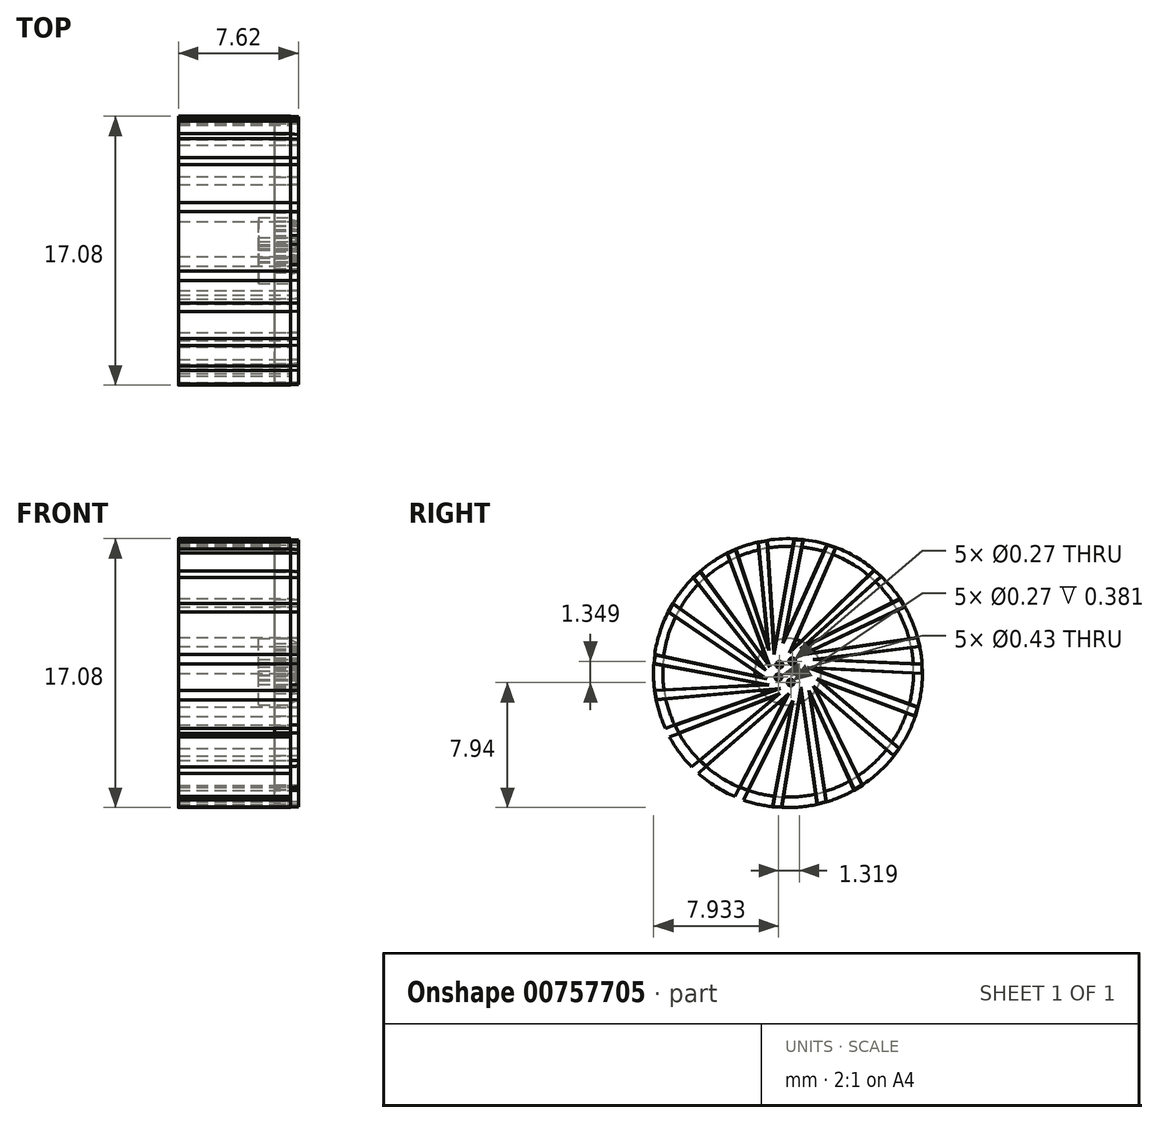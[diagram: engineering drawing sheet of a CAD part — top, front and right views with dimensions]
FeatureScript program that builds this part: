
annotation { "Feature Type Name" : "Feature", "Feature Type Description" : "" }
export const myFeature = defineFeature(function(context is Context, id is Id, definition is map)
    precondition{}
    {
        {
            var Q0;
            Q0=qCreatedBy(makeId("Right.planeOp"),FACE);
            var sketch = newSketch(context, id + "F0", { "sketchPlane" : qUnion([Q0])});
            skCircle(sketch, "E0", {"center": v(-0.01, -0.1) * mm, "radius": 8.54 * mm});
            skCircle(sketch, "E1", {"center": v(0, 0) * mm, "radius": 2.1 * mm});
            skCircle(sketch, "E2", {"center": v(0, 0) * mm, "radius": 7.96 * mm});
            skLineSegment(sketch, "E3", {"start": v(-0.39, -8.62) * mm, "end": v(0.81, -1.16) * mm});
            skLineSegment(sketch, "E4", {"start": v(0.81, -1.16) * mm, "end": v(1.84, -8.43) * mm});
            skLineSegment(sketch, "E5", {"start": v(2.43, -8.27) * mm, "end": v(1.38, -1.38) * mm});
            skLineSegment(sketch, "E6", {"start": v(1.38, -1.38) * mm, "end": v(4.19, -7.53) * mm});
            skLineSegment(sketch, "E7", {"start": v(-1, -8.58) * mm, "end": v(0.24, -2) * mm});
            skLineSegment(sketch, "E8", {"start": v(0.24, -2) * mm, "end": v(-2.83, -8.16) * mm});
            skLineSegment(sketch, "E9", {"start": v(-2.83, -8.16) * mm, "end": v(-3.4, -7.93) * mm});
            skLineSegment(sketch, "E10", {"start": v(-3.4, -7.93) * mm, "end": v(-0.05, -1.48) * mm});
            skLineSegment(sketch, "E11", {"start": v(-0.05, -1.48) * mm, "end": v(-5.7, -6.46) * mm});
            skLineSegment(sketch, "E12", {"start": v(-5.7, -6.46) * mm, "end": v(-6.14, -6.04) * mm});
            skLineSegment(sketch, "E13", {"start": v(-6.14, -6.04) * mm, "end": v(-0.66, -1.47) * mm});
            skLineSegment(sketch, "E14", {"start": v(-0.66, -1.47) * mm, "end": v(-7.53, -4.14) * mm});
            skLineSegment(sketch, "E15", {"start": v(-7.53, -4.14) * mm, "end": v(-7.8, -3.6) * mm});
            skLineSegment(sketch, "E16", {"start": v(-7.8, -3.6) * mm, "end": v(-0.7, -1.1) * mm});
            skLineSegment(sketch, "E17", {"start": v(-0.7, -1.1) * mm, "end": v(-8.39, -1.78) * mm});
            skLineSegment(sketch, "E18", {"start": v(-8.48, -1.18) * mm, "end": v(-1.45, -0.82) * mm});
            skLineSegment(sketch, "E19", {"start": v(-1.45, -0.82) * mm, "end": v(-8.53, 0.5) * mm});
            skLineSegment(sketch, "E20", {"start": v(-8.47, 1.1) * mm, "end": v(-1.46, -0.4) * mm});
            skLineSegment(sketch, "E21", {"start": v(-1.46, -0.4) * mm, "end": v(-7.62, 3.8) * mm});
            skLineSegment(sketch, "E22", {"start": v(-7.32, 4.33) * mm, "end": v(-1.54, 0.2) * mm});
            skLineSegment(sketch, "E23", {"start": v(-1.54, 0.2) * mm, "end": v(-6.03, 5.97) * mm});
            skLineSegment(sketch, "E24", {"start": v(-5.58, 6.38) * mm, "end": v(-1.25, 0.47) * mm});
            skLineSegment(sketch, "E25", {"start": v(4.7, -7.2) * mm, "end": v(1.68, -1) * mm});
            skLineSegment(sketch, "E26", {"start": v(1.68, -1) * mm, "end": v(6.7, -5.36) * mm});
            skLineSegment(sketch, "E27", {"start": v(7.06, -4.87) * mm, "end": v(1.98, -0.54) * mm});
            skLineSegment(sketch, "E28", {"start": v(1.98, -0.54) * mm, "end": v(8.07, -2.83) * mm});
            skLineSegment(sketch, "E29", {"start": v(8.5, 0.48) * mm, "end": v(1.87, 0.78) * mm});
            skLineSegment(sketch, "E30", {"start": v(1.87, 0.78) * mm, "end": v(8.36, 1.6) * mm});
            skLineSegment(sketch, "E31", {"start": v(8.22, 2.19) * mm, "end": v(1.05, 1.12) * mm});
            skLineSegment(sketch, "E32", {"start": v(1.05, 1.12) * mm, "end": v(7.42, 4.12) * mm});
            skLineSegment(sketch, "E33", {"start": v(7.1, 4.64) * mm, "end": v(0.95, 1.57) * mm});
            skLineSegment(sketch, "E34", {"start": v(0.95, 1.57) * mm, "end": v(5.92, 6.05) * mm});
            skLineSegment(sketch, "E35", {"start": v(5.46, 6.46) * mm, "end": v(0.17, 1.3) * mm});
            skLineSegment(sketch, "E36", {"start": v(0.17, 1.3) * mm, "end": v(3.04, 7.88) * mm});
            skLineSegment(sketch, "E37", {"start": v(2.47, 8.08) * mm, "end": v(-0.26, 2.01) * mm});
            skLineSegment(sketch, "E38", {"start": v(-0.26, 2.01) * mm, "end": v(0.99, 8.39) * mm});
            skLineSegment(sketch, "E39", {"start": v(0.38, 8.39) * mm, "end": v(-0.88, 1.31) * mm});
            skLineSegment(sketch, "E40", {"start": v(-0.88, 1.31) * mm, "end": v(-1.3, 8.35) * mm});
            skLineSegment(sketch, "E41", {"start": v(-1.9, 8.24) * mm, "end": v(-1.28, 1.57) * mm});
            skLineSegment(sketch, "E42", {"start": v(-1.28, 1.57) * mm, "end": v(-3.32, 7.78) * mm});
            skLineSegment(sketch, "E43", {"start": v(-3.87, 7.53) * mm, "end": v(-1.25, 0.47) * mm});
            skLineSegment(sketch, "E44", {"start": v(-1.9, 8.24) * mm, "end": v(-1.3, 8.35) * mm});
            skLineSegment(sketch, "E45", {"start": v(0.38, 8.39) * mm, "end": v(0.99, 8.39) * mm});
            skLineSegment(sketch, "E46", {"start": v(2.47, 8.08) * mm, "end": v(3.04, 7.88) * mm});
            skLineSegment(sketch, "E47", {"start": v(-3.32, 7.78) * mm, "end": v(-3.87, 7.53) * mm});
            skLineSegment(sketch, "E48", {"start": v(-5.58, 6.38) * mm, "end": v(-6.03, 5.97) * mm});
            skLineSegment(sketch, "E49", {"start": v(-7.32, 4.33) * mm, "end": v(-7.62, 3.8) * mm});
            skLineSegment(sketch, "E50", {"start": v(-7.8, -3.6) * mm, "end": v(-7.53, -4.14) * mm});
            skLineSegment(sketch, "E51", {"start": v(-6.14, -6.04) * mm, "end": v(-5.7, -6.46) * mm});
            skLineSegment(sketch, "E52", {"start": v(-3.4, -7.93) * mm, "end": v(-2.83, -8.16) * mm});
            skLineSegment(sketch, "E53", {"start": v(-1, -8.58) * mm, "end": v(-0.39, -8.62) * mm});
            skLineSegment(sketch, "E54", {"start": v(1.84, -8.43) * mm, "end": v(2.43, -8.27) * mm});
            skLineSegment(sketch, "E55", {"start": v(4.19, -7.53) * mm, "end": v(4.7, -7.2) * mm});
            skLineSegment(sketch, "E56", {"start": v(6.7, -5.36) * mm, "end": v(7.06, -4.87) * mm});
            skLineSegment(sketch, "E57", {"start": v(8.53, -0.13) * mm, "end": v(8.5, 0.48) * mm});
            skLineSegment(sketch, "E58", {"start": v(8.36, 1.6) * mm, "end": v(8.22, 2.19) * mm});
            skLineSegment(sketch, "E59", {"start": v(7.1, 4.64) * mm, "end": v(7.42, 4.12) * mm});
            skLineSegment(sketch, "E60", {"start": v(5.46, 6.46) * mm, "end": v(5.92, 6.05) * mm});
            skLineSegment(sketch, "E61", {"start": v(-8.47, 1.1) * mm, "end": v(-8.53, 0.5) * mm});
            skLineSegment(sketch, "E62", {"start": v(-8.39, -1.78) * mm, "end": v(-8.48, -1.18) * mm});
            skLineSegment(sketch, "E63", {"start": v(1.4, 0.23) * mm, "end": v(8.25, -2.25) * mm});
            skLineSegment(sketch, "E64", {"start": v(1.4, 0.23) * mm, "end": v(8.53, -0.13) * mm});
            skLineSegment(sketch, "E65", {"start": v(8.25, -2.25) * mm, "end": v(8.07, -2.83) * mm});
            skCircle(sketch, "E66", {"center": v(0, 0) * mm, "radius": 0.52 * mm});
            skCircle(sketch, "E67", {"center": v(0.26, 0.66) * mm, "radius": 0.19 * mm});
            skCircle(sketch, "E68", {"center": v(-0.55, 0.44) * mm, "radius": 0.19 * mm});
            skCircle(sketch, "E69", {"center": v(0.7, -0.1) * mm, "radius": 0.19 * mm});
            skCircle(sketch, "E70", {"center": v(-0.62, -0.35) * mm, "radius": 0.19 * mm});
            skCircle(sketch, "E71", {"center": v(0.16, -0.69) * mm, "radius": 0.19 * mm});
            skCircle(sketch, "E72", {"center": v(0.26, 0.66) * mm, "radius": 0.13 * mm});
            skCircle(sketch, "E73", {"center": v(-0.55, 0.44) * mm, "radius": 0.13 * mm});
            skCircle(sketch, "E74", {"center": v(-0.62, -0.35) * mm, "radius": 0.13 * mm});
            skCircle(sketch, "E75", {"center": v(0.16, -0.69) * mm, "radius": 0.13 * mm});
            skCircle(sketch, "E76", {"center": v(0.7, -0.1) * mm, "radius": 0.13 * mm});
            skLineSegment(sketch, "E77", {"start": v(-2, -1.56) * mm, "end": v(-1.87, -1.94) * mm});
            skLineSegment(sketch, "E78", {"start": v(-1.64, -2.3) * mm, "end": v(-1.36, -2.64) * mm});
            skLineSegment(sketch, "E79", {"start": v(-0.76, -2.86) * mm, "end": v(-0.3, -3.1) * mm});
            skLineSegment(sketch, "E80", {"start": v(0.04, -3.1) * mm, "end": v(0.49, -3.18) * mm});
            skLineSegment(sketch, "E81", {"start": v(1.1, -3.26) * mm, "end": v(1.66, -3.18) * mm});
            skLineSegment(sketch, "E82", {"start": v(2.12, -2.99) * mm, "end": v(2.55, -2.78) * mm});
            skLineSegment(sketch, "E83", {"start": v(3.07, -2.21) * mm, "end": v(3.44, -1.78) * mm});
            skLineSegment(sketch, "E84", {"start": v(3.64, -1.17) * mm, "end": v(3.74, -0.61) * mm});
            skLineSegment(sketch, "E85", {"start": v(-2.23, -1.23) * mm, "end": v(-2.25, -0.86) * mm});
            skLineSegment(sketch, "E86", {"start": v(-2.49, -0.62) * mm, "end": v(-2.4, -0.2) * mm});
            skLineSegment(sketch, "E87", {"start": v(-2.6, 0.38) * mm, "end": v(-2.33, 0.76) * mm});
            skLineSegment(sketch, "E88", {"start": v(-2.26, 1.12) * mm, "end": v(-1.91, 1.37) * mm});
            skLineSegment(sketch, "E89", {"start": v(-1.76, 1.84) * mm, "end": v(-1.4, 1.96) * mm});
            skSolve(sketch);
        }
        {
            var Q0;
            {var subQ36=sQuery(id+"F0.wireOp",EDGE,"E67");Q0=makeQuery(id+"F0.imprint","IMPRINT",FACE,{"disambiguationData":[TD([[makeQuery(id+"F0.imprint","IMPRINT",EDGE,{"derivedFrom":subQ36}),-1.0]])]});}
            var Q1;
            {var subQ0=sQuery(id+"F0.wireOp",EDGE,"E32");var subQ1=sQuery(id+"F0.wireOp",EDGE,"E1");var subQ2=makeQuery(id+"F0.imprint","INTERSECT",VERTEX,{"derivedFrom":[subQ1,subQ0]});Q1=makeQuery(id+"F0.imprint","IMPRINT",FACE,{"disambiguationData":[TD([[makeQuery(id+"F0.imprint","IMPRINT",EDGE,{"disambiguationData":[TD([[subQ2,-1.0]])],"derivedFrom":subQ1}),-1.0]])]});}
            var Q2;
            {var subQ0=sQuery(id+"F0.wireOp",EDGE,"E34");var subQ1=sQuery(id+"F0.wireOp",EDGE,"E1");var subQ2=makeQuery(id+"F0.imprint","INTERSECT",VERTEX,{"derivedFrom":[subQ1,subQ0]});Q2=makeQuery(id+"F0.imprint","IMPRINT",FACE,{"disambiguationData":[TD([[makeQuery(id+"F0.imprint","IMPRINT",EDGE,{"disambiguationData":[TD([[subQ2,-1.0]])],"derivedFrom":subQ1}),-1.0]])]});}
            var Q3;
            {var subQ0=sQuery(id+"F0.wireOp",EDGE,"E36");var subQ1=sQuery(id+"F0.wireOp",EDGE,"E1");var subQ2=makeQuery(id+"F0.imprint","INTERSECT",VERTEX,{"derivedFrom":[subQ1,subQ0]});Q3=makeQuery(id+"F0.imprint","IMPRINT",FACE,{"disambiguationData":[TD([[makeQuery(id+"F0.imprint","IMPRINT",EDGE,{"disambiguationData":[TD([[subQ2,-1.0]])],"derivedFrom":subQ1}),-1.0]])]});}
            var Q4;
            {var subQ0=sQuery(id+"F0.wireOp",EDGE,"E38");var subQ1=sQuery(id+"F0.wireOp",EDGE,"E1");var subQ2=makeQuery(id+"F0.imprint","INTERSECT",VERTEX,{"derivedFrom":[subQ1,subQ0]});Q4=makeQuery(id+"F0.imprint","IMPRINT",FACE,{"disambiguationData":[TD([[makeQuery(id+"F0.imprint","IMPRINT",EDGE,{"disambiguationData":[TD([[subQ2,-1.0]])],"derivedFrom":subQ1}),-1.0]])]});}
            var Q5;
            {var subQ0=sQuery(id+"F0.wireOp",EDGE,"E30");var subQ1=sQuery(id+"F0.wireOp",EDGE,"E1");var subQ2=makeQuery(id+"F0.imprint","INTERSECT",VERTEX,{"derivedFrom":[subQ1,subQ0]});Q5=makeQuery(id+"F0.imprint","IMPRINT",FACE,{"disambiguationData":[TD([[makeQuery(id+"F0.imprint","IMPRINT",EDGE,{"disambiguationData":[TD([[subQ2,-1.0]])],"derivedFrom":subQ1}),-1.0]])]});}
            var Q6;
            {var subQ0=sQuery(id+"F0.wireOp",EDGE,"E29");var subQ1=sQuery(id+"F0.wireOp",EDGE,"E1");var subQ2=makeQuery(id+"F0.imprint","INTERSECT",VERTEX,{"derivedFrom":[subQ1,subQ0]});Q6=makeQuery(id+"F0.imprint","IMPRINT",FACE,{"disambiguationData":[TD([[makeQuery(id+"F0.imprint","IMPRINT",EDGE,{"disambiguationData":[TD([[subQ2,1.0]])],"derivedFrom":subQ1}),-1.0]])]});}
            var Q7;
            {var subQ0=sQuery(id+"F0.wireOp",EDGE,"E28");var subQ1=sQuery(id+"F0.wireOp",EDGE,"E1");var subQ2=makeQuery(id+"F0.imprint","INTERSECT",VERTEX,{"derivedFrom":[subQ1,subQ0]});Q7=makeQuery(id+"F0.imprint","IMPRINT",FACE,{"disambiguationData":[TD([[makeQuery(id+"F0.imprint","IMPRINT",EDGE,{"disambiguationData":[TD([[subQ2,-1.0]])],"derivedFrom":subQ1}),-1.0]])]});}
            var Q8;
            {var subQ0=sQuery(id+"F0.wireOp",EDGE,"E26");var subQ1=sQuery(id+"F0.wireOp",EDGE,"E1");var subQ2=makeQuery(id+"F0.imprint","INTERSECT",VERTEX,{"derivedFrom":[subQ1,subQ0]});Q8=makeQuery(id+"F0.imprint","IMPRINT",FACE,{"disambiguationData":[TD([[makeQuery(id+"F0.imprint","IMPRINT",EDGE,{"disambiguationData":[TD([[subQ2,-1.0]])],"derivedFrom":subQ1}),-1.0]])]});}
            var Q9;
            {var subQ0=sQuery(id+"F0.wireOp",EDGE,"E6");var subQ1=sQuery(id+"F0.wireOp",EDGE,"E1");var subQ2=makeQuery(id+"F0.imprint","INTERSECT",VERTEX,{"derivedFrom":[subQ1,subQ0]});Q9=makeQuery(id+"F0.imprint","IMPRINT",FACE,{"disambiguationData":[TD([[makeQuery(id+"F0.imprint","IMPRINT",EDGE,{"disambiguationData":[TD([[subQ2,-1.0]])],"derivedFrom":subQ1}),-1.0]])]});}
            var Q10;
            {var subQ0=sQuery(id+"F0.wireOp",EDGE,"E4");var subQ1=sQuery(id+"F0.wireOp",EDGE,"E1");var subQ2=makeQuery(id+"F0.imprint","INTERSECT",VERTEX,{"derivedFrom":[subQ1,subQ0]});Q10=makeQuery(id+"F0.imprint","IMPRINT",FACE,{"disambiguationData":[TD([[makeQuery(id+"F0.imprint","IMPRINT",EDGE,{"disambiguationData":[TD([[subQ2,-1.0]])],"derivedFrom":subQ1}),-1.0]])]});}
            var Q11;
            {var subQ0=sQuery(id+"F0.wireOp",EDGE,"E7");var subQ1=sQuery(id+"F0.wireOp",EDGE,"E1");var subQ2=makeQuery(id+"F0.imprint","INTERSECT",VERTEX,{"derivedFrom":[subQ1,subQ0]});Q11=makeQuery(id+"F0.imprint","IMPRINT",FACE,{"disambiguationData":[TD([[makeQuery(id+"F0.imprint","IMPRINT",EDGE,{"disambiguationData":[TD([[subQ2,-1.0]])],"derivedFrom":subQ1}),-1.0]])]});}
            var Q12;
            {var subQ0=sQuery(id+"F0.wireOp",EDGE,"E10");var subQ1=sQuery(id+"F0.wireOp",EDGE,"E1");var subQ2=makeQuery(id+"F0.imprint","INTERSECT",VERTEX,{"derivedFrom":[subQ1,subQ0]});Q12=makeQuery(id+"F0.imprint","IMPRINT",FACE,{"disambiguationData":[TD([[makeQuery(id+"F0.imprint","IMPRINT",EDGE,{"disambiguationData":[TD([[subQ2,-1.0]])],"derivedFrom":subQ1}),-1.0]])]});}
            var Q13;
            {var subQ0=sQuery(id+"F0.wireOp",EDGE,"E13");var subQ1=sQuery(id+"F0.wireOp",EDGE,"E1");var subQ2=makeQuery(id+"F0.imprint","INTERSECT",VERTEX,{"derivedFrom":[subQ1,subQ0]});Q13=makeQuery(id+"F0.imprint","IMPRINT",FACE,{"disambiguationData":[TD([[makeQuery(id+"F0.imprint","IMPRINT",EDGE,{"disambiguationData":[TD([[subQ2,-1.0]])],"derivedFrom":subQ1}),-1.0]])]});}
            var Q14;
            {var subQ0=sQuery(id+"F0.wireOp",EDGE,"E16");var subQ1=sQuery(id+"F0.wireOp",EDGE,"E1");var subQ2=makeQuery(id+"F0.imprint","INTERSECT",VERTEX,{"derivedFrom":[subQ1,subQ0]});Q14=makeQuery(id+"F0.imprint","IMPRINT",FACE,{"disambiguationData":[TD([[makeQuery(id+"F0.imprint","IMPRINT",EDGE,{"disambiguationData":[TD([[subQ2,-1.0]])],"derivedFrom":subQ1}),-1.0]])]});}
            var Q15;
            {var subQ0=sQuery(id+"F0.wireOp",EDGE,"E18");var subQ1=sQuery(id+"F0.wireOp",EDGE,"E1");var subQ2=makeQuery(id+"F0.imprint","INTERSECT",VERTEX,{"derivedFrom":[subQ1,subQ0]});Q15=makeQuery(id+"F0.imprint","IMPRINT",FACE,{"disambiguationData":[TD([[makeQuery(id+"F0.imprint","IMPRINT",EDGE,{"disambiguationData":[TD([[subQ2,-1.0]])],"derivedFrom":subQ1}),-1.0]])]});}
            var Q16;
            {var subQ0=sQuery(id+"F0.wireOp",EDGE,"E20");var subQ1=sQuery(id+"F0.wireOp",EDGE,"E1");var subQ2=makeQuery(id+"F0.imprint","INTERSECT",VERTEX,{"derivedFrom":[subQ1,subQ0]});Q16=makeQuery(id+"F0.imprint","IMPRINT",FACE,{"disambiguationData":[TD([[makeQuery(id+"F0.imprint","IMPRINT",EDGE,{"disambiguationData":[TD([[subQ2,-1.0]])],"derivedFrom":subQ1}),-1.0]])]});}
            var Q17;
            {var subQ0=sQuery(id+"F0.wireOp",EDGE,"E22");var subQ1=sQuery(id+"F0.wireOp",EDGE,"E1");var subQ2=makeQuery(id+"F0.imprint","INTERSECT",VERTEX,{"derivedFrom":[subQ1,subQ0]});Q17=makeQuery(id+"F0.imprint","IMPRINT",FACE,{"disambiguationData":[TD([[makeQuery(id+"F0.imprint","IMPRINT",EDGE,{"disambiguationData":[TD([[subQ2,-1.0]])],"derivedFrom":subQ1}),-1.0]])]});}
            var Q18;
            {var subQ0=sQuery(id+"F0.wireOp",EDGE,"E24");var subQ1=sQuery(id+"F0.wireOp",EDGE,"E1");var subQ2=makeQuery(id+"F0.imprint","INTERSECT",VERTEX,{"derivedFrom":[subQ1,subQ0]});Q18=makeQuery(id+"F0.imprint","IMPRINT",FACE,{"disambiguationData":[TD([[makeQuery(id+"F0.imprint","IMPRINT",EDGE,{"disambiguationData":[TD([[subQ2,-1.0]])],"derivedFrom":subQ1}),-1.0]])]});}
            var Q19;
            {var subQ0=sQuery(id+"F0.wireOp",EDGE,"E42");var subQ1=sQuery(id+"F0.wireOp",EDGE,"E1");var subQ2=makeQuery(id+"F0.imprint","INTERSECT",VERTEX,{"derivedFrom":[subQ1,subQ0]});Q19=makeQuery(id+"F0.imprint","IMPRINT",FACE,{"disambiguationData":[TD([[makeQuery(id+"F0.imprint","IMPRINT",EDGE,{"disambiguationData":[TD([[subQ2,-1.0]])],"derivedFrom":subQ1}),-1.0]])]});}
            var Q20;
            {var subQ0=sQuery(id+"F0.wireOp",EDGE,"E40");var subQ1=sQuery(id+"F0.wireOp",EDGE,"E1");var subQ2=makeQuery(id+"F0.imprint","INTERSECT",VERTEX,{"derivedFrom":[subQ1,subQ0]});Q20=makeQuery(id+"F0.imprint","IMPRINT",FACE,{"disambiguationData":[TD([[makeQuery(id+"F0.imprint","IMPRINT",EDGE,{"disambiguationData":[TD([[subQ2,-1.0]])],"derivedFrom":subQ1}),-1.0]])]});}
            var Q21;
            {var subQ5=sQuery(id+"F0.wireOp",EDGE,"E57");Q21=makeQuery(id+"F0.imprint","IMPRINT",FACE,{"disambiguationData":[TD([[makeQuery(id+"F0.imprint","IMPRINT",EDGE,{"derivedFrom":subQ5}),1.0]])]});}
            var Q22;
            {var subQ5=sQuery(id+"F0.wireOp",EDGE,"E58");Q22=makeQuery(id+"F0.imprint","IMPRINT",FACE,{"disambiguationData":[TD([[makeQuery(id+"F0.imprint","IMPRINT",EDGE,{"derivedFrom":subQ5}),1.0]])]});}
            var Q23;
            {var subQ5=sQuery(id+"F0.wireOp",EDGE,"E59");Q23=makeQuery(id+"F0.imprint","IMPRINT",FACE,{"disambiguationData":[TD([[makeQuery(id+"F0.imprint","IMPRINT",EDGE,{"derivedFrom":subQ5}),-1.0]])]});}
            var Q24;
            {var subQ5=sQuery(id+"F0.wireOp",EDGE,"E60");Q24=makeQuery(id+"F0.imprint","IMPRINT",FACE,{"disambiguationData":[TD([[makeQuery(id+"F0.imprint","IMPRINT",EDGE,{"derivedFrom":subQ5}),-1.0]])]});}
            var Q25;
            {var subQ5=sQuery(id+"F0.wireOp",EDGE,"E46");Q25=makeQuery(id+"F0.imprint","IMPRINT",FACE,{"disambiguationData":[TD([[makeQuery(id+"F0.imprint","IMPRINT",EDGE,{"derivedFrom":subQ5}),-1.0]])]});}
            var Q26;
            {var subQ5=sQuery(id+"F0.wireOp",EDGE,"E45");Q26=makeQuery(id+"F0.imprint","IMPRINT",FACE,{"disambiguationData":[TD([[makeQuery(id+"F0.imprint","IMPRINT",EDGE,{"derivedFrom":subQ5}),-1.0]])]});}
            var Q27;
            {var subQ5=sQuery(id+"F0.wireOp",EDGE,"E44");Q27=makeQuery(id+"F0.imprint","IMPRINT",FACE,{"disambiguationData":[TD([[makeQuery(id+"F0.imprint","IMPRINT",EDGE,{"derivedFrom":subQ5}),-1.0]])]});}
            var Q28;
            {var subQ5=sQuery(id+"F0.wireOp",EDGE,"E47");Q28=makeQuery(id+"F0.imprint","IMPRINT",FACE,{"disambiguationData":[TD([[makeQuery(id+"F0.imprint","IMPRINT",EDGE,{"derivedFrom":subQ5}),1.0]])]});}
            var Q29;
            {var subQ5=sQuery(id+"F0.wireOp",EDGE,"E48");Q29=makeQuery(id+"F0.imprint","IMPRINT",FACE,{"disambiguationData":[TD([[makeQuery(id+"F0.imprint","IMPRINT",EDGE,{"derivedFrom":subQ5}),1.0]])]});}
            var Q30;
            {var subQ5=sQuery(id+"F0.wireOp",EDGE,"E49");Q30=makeQuery(id+"F0.imprint","IMPRINT",FACE,{"disambiguationData":[TD([[makeQuery(id+"F0.imprint","IMPRINT",EDGE,{"derivedFrom":subQ5}),1.0]])]});}
            var Q31;
            {var subQ5=sQuery(id+"F0.wireOp",EDGE,"E61");Q31=makeQuery(id+"F0.imprint","IMPRINT",FACE,{"disambiguationData":[TD([[makeQuery(id+"F0.imprint","IMPRINT",EDGE,{"derivedFrom":subQ5}),1.0]])]});}
            var Q32;
            {var subQ5=sQuery(id+"F0.wireOp",EDGE,"E62");Q32=makeQuery(id+"F0.imprint","IMPRINT",FACE,{"disambiguationData":[TD([[makeQuery(id+"F0.imprint","IMPRINT",EDGE,{"derivedFrom":subQ5}),-1.0]])]});}
            var Q33;
            {var subQ5=sQuery(id+"F0.wireOp",EDGE,"E50");Q33=makeQuery(id+"F0.imprint","IMPRINT",FACE,{"disambiguationData":[TD([[makeQuery(id+"F0.imprint","IMPRINT",EDGE,{"derivedFrom":subQ5}),1.0]])]});}
            var Q34;
            {var subQ5=sQuery(id+"F0.wireOp",EDGE,"E51");Q34=makeQuery(id+"F0.imprint","IMPRINT",FACE,{"disambiguationData":[TD([[makeQuery(id+"F0.imprint","IMPRINT",EDGE,{"derivedFrom":subQ5}),1.0]])]});}
            var Q35;
            {var subQ5=sQuery(id+"F0.wireOp",EDGE,"E52");Q35=makeQuery(id+"F0.imprint","IMPRINT",FACE,{"disambiguationData":[TD([[makeQuery(id+"F0.imprint","IMPRINT",EDGE,{"derivedFrom":subQ5}),1.0]])]});}
            var Q36;
            {var subQ5=sQuery(id+"F0.wireOp",EDGE,"E53");Q36=makeQuery(id+"F0.imprint","IMPRINT",FACE,{"disambiguationData":[TD([[makeQuery(id+"F0.imprint","IMPRINT",EDGE,{"derivedFrom":subQ5}),1.0]])]});}
            var Q37;
            {var subQ5=sQuery(id+"F0.wireOp",EDGE,"E54");Q37=makeQuery(id+"F0.imprint","IMPRINT",FACE,{"disambiguationData":[TD([[makeQuery(id+"F0.imprint","IMPRINT",EDGE,{"derivedFrom":subQ5}),1.0]])]});}
            var Q38;
            {var subQ5=sQuery(id+"F0.wireOp",EDGE,"E55");Q38=makeQuery(id+"F0.imprint","IMPRINT",FACE,{"disambiguationData":[TD([[makeQuery(id+"F0.imprint","IMPRINT",EDGE,{"derivedFrom":subQ5}),1.0]])]});}
            var Q39;
            {var subQ5=sQuery(id+"F0.wireOp",EDGE,"E56");Q39=makeQuery(id+"F0.imprint","IMPRINT",FACE,{"disambiguationData":[TD([[makeQuery(id+"F0.imprint","IMPRINT",EDGE,{"derivedFrom":subQ5}),1.0]])]});}
            var Q40;
            {var subQ5=sQuery(id+"F0.wireOp",EDGE,"E65");Q40=makeQuery(id+"F0.imprint","IMPRINT",FACE,{"disambiguationData":[TD([[makeQuery(id+"F0.imprint","IMPRINT",EDGE,{"derivedFrom":subQ5}),-1.0]])]});}
            var Q41;
            {var subQ0=sQuery(id+"F0.wireOp",EDGE,"E66");var subQ4=makeQuery(id+"F0.imprint","INTERSECT",VERTEX,{"derivedFrom":[subQ0,sQuery(id+"F0.wireOp",EDGE,"E68")]});Q41=makeQuery(id+"F0.imprint","IMPRINT",FACE,{"disambiguationData":[TD([[makeQuery(id+"F0.imprint","IMPRINT",EDGE,{"disambiguationData":[TD([[subQ4,1.0]])],"derivedFrom":subQ0}),1.0]])]});}
            var Q42;
            {var subQ5=sQuery(id+"F0.wireOp",EDGE,"E84");Q42=makeQuery(id+"F0.imprint","IMPRINT",FACE,{"disambiguationData":[TD([[makeQuery(id+"F0.imprint","IMPRINT",EDGE,{"derivedFrom":subQ5}),-1.0]])]});}
            var Q43;
            {var subQ5=sQuery(id+"F0.wireOp",EDGE,"E83");Q43=makeQuery(id+"F0.imprint","IMPRINT",FACE,{"disambiguationData":[TD([[makeQuery(id+"F0.imprint","IMPRINT",EDGE,{"derivedFrom":subQ5}),-1.0]])]});}
            var Q44;
            {var subQ5=sQuery(id+"F0.wireOp",EDGE,"E82");Q44=makeQuery(id+"F0.imprint","IMPRINT",FACE,{"disambiguationData":[TD([[makeQuery(id+"F0.imprint","IMPRINT",EDGE,{"derivedFrom":subQ5}),-1.0]])]});}
            var Q45;
            {var subQ5=sQuery(id+"F0.wireOp",EDGE,"E81");Q45=makeQuery(id+"F0.imprint","IMPRINT",FACE,{"disambiguationData":[TD([[makeQuery(id+"F0.imprint","IMPRINT",EDGE,{"derivedFrom":subQ5}),-1.0]])]});}
            var Q46;
            {var subQ5=sQuery(id+"F0.wireOp",EDGE,"E80");Q46=makeQuery(id+"F0.imprint","IMPRINT",FACE,{"disambiguationData":[TD([[makeQuery(id+"F0.imprint","IMPRINT",EDGE,{"derivedFrom":subQ5}),-1.0]])]});}
            var Q47;
            {var subQ5=sQuery(id+"F0.wireOp",EDGE,"E79");Q47=makeQuery(id+"F0.imprint","IMPRINT",FACE,{"disambiguationData":[TD([[makeQuery(id+"F0.imprint","IMPRINT",EDGE,{"derivedFrom":subQ5}),-1.0]])]});}
            var Q48;
            {var subQ5=sQuery(id+"F0.wireOp",EDGE,"E78");Q48=makeQuery(id+"F0.imprint","IMPRINT",FACE,{"disambiguationData":[TD([[makeQuery(id+"F0.imprint","IMPRINT",EDGE,{"derivedFrom":subQ5}),-1.0]])]});}
            var Q49;
            {var subQ5=sQuery(id+"F0.wireOp",EDGE,"E77");Q49=makeQuery(id+"F0.imprint","IMPRINT",FACE,{"disambiguationData":[TD([[makeQuery(id+"F0.imprint","IMPRINT",EDGE,{"derivedFrom":subQ5}),-1.0]])]});}
            var Q50;
            {var subQ5=sQuery(id+"F0.wireOp",EDGE,"E85");Q50=makeQuery(id+"F0.imprint","IMPRINT",FACE,{"disambiguationData":[TD([[makeQuery(id+"F0.imprint","IMPRINT",EDGE,{"derivedFrom":subQ5}),1.0]])]});}
            var Q51;
            {var subQ5=sQuery(id+"F0.wireOp",EDGE,"E87");Q51=makeQuery(id+"F0.imprint","IMPRINT",FACE,{"disambiguationData":[TD([[makeQuery(id+"F0.imprint","IMPRINT",EDGE,{"derivedFrom":subQ5}),1.0]])]});}
            var Q52;
            {var subQ5=sQuery(id+"F0.wireOp",EDGE,"E88");Q52=makeQuery(id+"F0.imprint","IMPRINT",FACE,{"disambiguationData":[TD([[makeQuery(id+"F0.imprint","IMPRINT",EDGE,{"derivedFrom":subQ5}),1.0]])]});}
            var Q53;
            {var subQ5=sQuery(id+"F0.wireOp",EDGE,"E89");Q53=makeQuery(id+"F0.imprint","IMPRINT",FACE,{"disambiguationData":[TD([[makeQuery(id+"F0.imprint","IMPRINT",EDGE,{"derivedFrom":subQ5}),1.0]])]});}
            extrude(context, id + "F1", {"entities" : qUnion([Q0, Q1, Q2, Q3, Q4, Q5, Q6, Q7, Q8, Q9, Q10, Q11, Q12, Q13, Q14, Q15, Q16, Q17, Q18, Q19, Q20, Q21, Q22, Q23, Q24, Q25, Q26, Q27, Q28, Q29, Q30, Q31, Q32, Q33, Q34, Q35, Q36, Q37, Q38, Q39, Q40, Q41, Q42, Q43, Q44, Q45, Q46, Q47, Q48, Q49, Q50, Q51, Q52, Q53]), "depth" : 0.5 * mm, "hasDraft" : true, "draftAngle" : 3 * degree, "draftPullDirection" : true, "offsetDistance" : 25.4 * mm});
        }
        {
            var Q0;
            Q0=makeQuery(id+"F0.imprint","IMPRINT",FACE,{"disambiguationData":[TD([[makeQuery(id+"F0.imprint","IMPRINT",EDGE,{"derivedFrom":sQuery(id+"F0.wireOp",EDGE,"E67")}),1.0]])]});
            var Q1;
            Q1=makeQuery(id+"F0.imprint","IMPRINT",FACE,{"disambiguationData":[TD([[makeQuery(id+"F0.imprint","IMPRINT",EDGE,{"derivedFrom":sQuery(id+"F0.wireOp",EDGE,"E68")}),1.0]])]});
            var Q2;
            Q2=makeQuery(id+"F0.imprint","IMPRINT",FACE,{"disambiguationData":[TD([[makeQuery(id+"F0.imprint","IMPRINT",EDGE,{"derivedFrom":sQuery(id+"F0.wireOp",EDGE,"E69")}),1.0]])]});
            var Q3;
            Q3=makeQuery(id+"F0.imprint","IMPRINT",FACE,{"disambiguationData":[TD([[makeQuery(id+"F0.imprint","IMPRINT",EDGE,{"derivedFrom":sQuery(id+"F0.wireOp",EDGE,"E71")}),1.0]])]});
            var Q4;
            Q4=makeQuery(id+"F0.imprint","IMPRINT",FACE,{"disambiguationData":[TD([[makeQuery(id+"F0.imprint","IMPRINT",EDGE,{"derivedFrom":sQuery(id+"F0.wireOp",EDGE,"E70")}),1.0]])]});
            extrude(context, id + "F2", {"entities" : qUnion([Q0, Q1, Q2, Q3, Q4]), "depth" : 0.38 * mm});
        }
        {
            var Q0;
            {var subQ3=sQuery(id+"F0.wireOp",EDGE,"E43");var subQ5=sQuery(id+"F0.wireOp",EDGE,"E2");var subQ6=makeQuery(id+"F0.imprint","INTERSECT",VERTEX,{"derivedFrom":[subQ5,subQ3]});Q0=makeQuery(id+"F0.imprint","IMPRINT",FACE,{"disambiguationData":[TD([[makeQuery(id+"F0.imprint","IMPRINT",EDGE,{"disambiguationData":[TD([[subQ6,-1.0]])],"derivedFrom":subQ5}),-1.0]])]});}
            var Q1;
            {var subQ5=sQuery(id+"F0.wireOp",EDGE,"E48");Q1=makeQuery(id+"F0.imprint","IMPRINT",FACE,{"disambiguationData":[TD([[makeQuery(id+"F0.imprint","IMPRINT",EDGE,{"derivedFrom":subQ5}),1.0]])]});}
            var Q2;
            {var subQ3=sQuery(id+"F0.wireOp",EDGE,"E23");var subQ5=sQuery(id+"F0.wireOp",EDGE,"E2");var subQ7=makeQuery(id+"F0.imprint","INTERSECT",VERTEX,{"derivedFrom":[subQ5,subQ3]});Q2=makeQuery(id+"F0.imprint","IMPRINT",FACE,{"disambiguationData":[TD([[makeQuery(id+"F0.imprint","IMPRINT",EDGE,{"disambiguationData":[TD([[subQ7,-1.0]])],"derivedFrom":subQ5}),-1.0]])]});}
            var Q3;
            {var subQ5=sQuery(id+"F0.wireOp",EDGE,"E49");Q3=makeQuery(id+"F0.imprint","IMPRINT",FACE,{"disambiguationData":[TD([[makeQuery(id+"F0.imprint","IMPRINT",EDGE,{"derivedFrom":subQ5}),1.0]])]});}
            var Q4;
            {var subQ3=sQuery(id+"F0.wireOp",EDGE,"E21");var subQ5=sQuery(id+"F0.wireOp",EDGE,"E2");var subQ7=makeQuery(id+"F0.imprint","INTERSECT",VERTEX,{"derivedFrom":[subQ5,subQ3]});Q4=makeQuery(id+"F0.imprint","IMPRINT",FACE,{"disambiguationData":[TD([[makeQuery(id+"F0.imprint","IMPRINT",EDGE,{"disambiguationData":[TD([[subQ7,-1.0]])],"derivedFrom":subQ5}),-1.0]])]});}
            var Q5;
            {var subQ5=sQuery(id+"F0.wireOp",EDGE,"E61");Q5=makeQuery(id+"F0.imprint","IMPRINT",FACE,{"disambiguationData":[TD([[makeQuery(id+"F0.imprint","IMPRINT",EDGE,{"derivedFrom":subQ5}),1.0]])]});}
            var Q6;
            {var subQ3=sQuery(id+"F0.wireOp",EDGE,"E19");var subQ5=sQuery(id+"F0.wireOp",EDGE,"E2");var subQ6=makeQuery(id+"F0.imprint","INTERSECT",VERTEX,{"derivedFrom":[subQ5,subQ3]});Q6=makeQuery(id+"F0.imprint","IMPRINT",FACE,{"disambiguationData":[TD([[makeQuery(id+"F0.imprint","IMPRINT",EDGE,{"disambiguationData":[TD([[subQ6,-1.0]])],"derivedFrom":subQ5}),-1.0]])]});}
            var Q7;
            {var subQ5=sQuery(id+"F0.wireOp",EDGE,"E62");Q7=makeQuery(id+"F0.imprint","IMPRINT",FACE,{"disambiguationData":[TD([[makeQuery(id+"F0.imprint","IMPRINT",EDGE,{"derivedFrom":subQ5}),-1.0]])]});}
            var Q8;
            {var subQ3=sQuery(id+"F0.wireOp",EDGE,"E17");var subQ5=sQuery(id+"F0.wireOp",EDGE,"E2");var subQ7=makeQuery(id+"F0.imprint","INTERSECT",VERTEX,{"derivedFrom":[subQ5,subQ3]});Q8=makeQuery(id+"F0.imprint","IMPRINT",FACE,{"disambiguationData":[TD([[makeQuery(id+"F0.imprint","IMPRINT",EDGE,{"disambiguationData":[TD([[subQ7,-1.0]])],"derivedFrom":subQ5}),-1.0]])]});}
            var Q9;
            {var subQ5=sQuery(id+"F0.wireOp",EDGE,"E50");Q9=makeQuery(id+"F0.imprint","IMPRINT",FACE,{"disambiguationData":[TD([[makeQuery(id+"F0.imprint","IMPRINT",EDGE,{"derivedFrom":subQ5}),1.0]])]});}
            var Q10;
            {var subQ3=sQuery(id+"F0.wireOp",EDGE,"E14");var subQ5=sQuery(id+"F0.wireOp",EDGE,"E2");var subQ6=makeQuery(id+"F0.imprint","INTERSECT",VERTEX,{"derivedFrom":[subQ5,subQ3]});Q10=makeQuery(id+"F0.imprint","IMPRINT",FACE,{"disambiguationData":[TD([[makeQuery(id+"F0.imprint","IMPRINT",EDGE,{"disambiguationData":[TD([[subQ6,-1.0]])],"derivedFrom":subQ5}),-1.0]])]});}
            var Q11;
            {var subQ5=sQuery(id+"F0.wireOp",EDGE,"E51");Q11=makeQuery(id+"F0.imprint","IMPRINT",FACE,{"disambiguationData":[TD([[makeQuery(id+"F0.imprint","IMPRINT",EDGE,{"derivedFrom":subQ5}),1.0]])]});}
            var Q12;
            {var subQ3=sQuery(id+"F0.wireOp",EDGE,"E11");var subQ5=sQuery(id+"F0.wireOp",EDGE,"E2");var subQ6=makeQuery(id+"F0.imprint","INTERSECT",VERTEX,{"derivedFrom":[subQ5,subQ3]});Q12=makeQuery(id+"F0.imprint","IMPRINT",FACE,{"disambiguationData":[TD([[makeQuery(id+"F0.imprint","IMPRINT",EDGE,{"disambiguationData":[TD([[subQ6,-1.0]])],"derivedFrom":subQ5}),-1.0]])]});}
            var Q13;
            {var subQ5=sQuery(id+"F0.wireOp",EDGE,"E52");Q13=makeQuery(id+"F0.imprint","IMPRINT",FACE,{"disambiguationData":[TD([[makeQuery(id+"F0.imprint","IMPRINT",EDGE,{"derivedFrom":subQ5}),1.0]])]});}
            var Q14;
            {var subQ3=sQuery(id+"F0.wireOp",EDGE,"E8");var subQ5=sQuery(id+"F0.wireOp",EDGE,"E2");var subQ6=makeQuery(id+"F0.imprint","INTERSECT",VERTEX,{"derivedFrom":[subQ5,subQ3]});Q14=makeQuery(id+"F0.imprint","IMPRINT",FACE,{"disambiguationData":[TD([[makeQuery(id+"F0.imprint","IMPRINT",EDGE,{"disambiguationData":[TD([[subQ6,-1.0]])],"derivedFrom":subQ5}),-1.0]])]});}
            var Q15;
            {var subQ5=sQuery(id+"F0.wireOp",EDGE,"E47");Q15=makeQuery(id+"F0.imprint","IMPRINT",FACE,{"disambiguationData":[TD([[makeQuery(id+"F0.imprint","IMPRINT",EDGE,{"derivedFrom":subQ5}),1.0]])]});}
            var Q16;
            {var subQ0=sQuery(id+"F0.wireOp",EDGE,"E41");var subQ5=sQuery(id+"F0.wireOp",EDGE,"E2");var subQ6=makeQuery(id+"F0.imprint","INTERSECT",VERTEX,{"derivedFrom":[subQ5,subQ0]});Q16=makeQuery(id+"F0.imprint","IMPRINT",FACE,{"disambiguationData":[TD([[makeQuery(id+"F0.imprint","IMPRINT",EDGE,{"disambiguationData":[TD([[subQ6,-1.0]])],"derivedFrom":subQ5}),-1.0]])]});}
            var Q17;
            {var subQ5=sQuery(id+"F0.wireOp",EDGE,"E44");Q17=makeQuery(id+"F0.imprint","IMPRINT",FACE,{"disambiguationData":[TD([[makeQuery(id+"F0.imprint","IMPRINT",EDGE,{"derivedFrom":subQ5}),-1.0]])]});}
            var Q18;
            {var subQ7=sQuery(id+"F0.wireOp",EDGE,"E45");Q18=makeQuery(id+"F0.imprint","IMPRINT",FACE,{"disambiguationData":[TD([[makeQuery(id+"F0.imprint","IMPRINT",EDGE,{"derivedFrom":subQ7}),1.0]])]});}
            var Q19;
            {var subQ5=sQuery(id+"F0.wireOp",EDGE,"E45");Q19=makeQuery(id+"F0.imprint","IMPRINT",FACE,{"disambiguationData":[TD([[makeQuery(id+"F0.imprint","IMPRINT",EDGE,{"derivedFrom":subQ5}),-1.0]])]});}
            var Q20;
            {var subQ0=sQuery(id+"F0.wireOp",EDGE,"E37");var subQ5=sQuery(id+"F0.wireOp",EDGE,"E2");var subQ7=makeQuery(id+"F0.imprint","INTERSECT",VERTEX,{"derivedFrom":[subQ5,subQ0]});Q20=makeQuery(id+"F0.imprint","IMPRINT",FACE,{"disambiguationData":[TD([[makeQuery(id+"F0.imprint","IMPRINT",EDGE,{"disambiguationData":[TD([[subQ7,-1.0]])],"derivedFrom":subQ5}),-1.0]])]});}
            var Q21;
            {var subQ5=sQuery(id+"F0.wireOp",EDGE,"E46");Q21=makeQuery(id+"F0.imprint","IMPRINT",FACE,{"disambiguationData":[TD([[makeQuery(id+"F0.imprint","IMPRINT",EDGE,{"derivedFrom":subQ5}),-1.0]])]});}
            var Q22;
            {var subQ0=sQuery(id+"F0.wireOp",EDGE,"E35");var subQ5=sQuery(id+"F0.wireOp",EDGE,"E2");var subQ6=makeQuery(id+"F0.imprint","INTERSECT",VERTEX,{"derivedFrom":[subQ5,subQ0]});Q22=makeQuery(id+"F0.imprint","IMPRINT",FACE,{"disambiguationData":[TD([[makeQuery(id+"F0.imprint","IMPRINT",EDGE,{"disambiguationData":[TD([[subQ6,-1.0]])],"derivedFrom":subQ5}),-1.0]])]});}
            var Q23;
            {var subQ5=sQuery(id+"F0.wireOp",EDGE,"E60");Q23=makeQuery(id+"F0.imprint","IMPRINT",FACE,{"disambiguationData":[TD([[makeQuery(id+"F0.imprint","IMPRINT",EDGE,{"derivedFrom":subQ5}),-1.0]])]});}
            var Q24;
            {var subQ0=sQuery(id+"F0.wireOp",EDGE,"E33");var subQ5=sQuery(id+"F0.wireOp",EDGE,"E2");var subQ6=makeQuery(id+"F0.imprint","INTERSECT",VERTEX,{"derivedFrom":[subQ5,subQ0]});Q24=makeQuery(id+"F0.imprint","IMPRINT",FACE,{"disambiguationData":[TD([[makeQuery(id+"F0.imprint","IMPRINT",EDGE,{"disambiguationData":[TD([[subQ6,-1.0]])],"derivedFrom":subQ5}),-1.0]])]});}
            var Q25;
            {var subQ5=sQuery(id+"F0.wireOp",EDGE,"E59");Q25=makeQuery(id+"F0.imprint","IMPRINT",FACE,{"disambiguationData":[TD([[makeQuery(id+"F0.imprint","IMPRINT",EDGE,{"derivedFrom":subQ5}),-1.0]])]});}
            var Q26;
            {var subQ0=sQuery(id+"F0.wireOp",EDGE,"E31");var subQ5=sQuery(id+"F0.wireOp",EDGE,"E2");var subQ6=makeQuery(id+"F0.imprint","INTERSECT",VERTEX,{"derivedFrom":[subQ5,subQ0]});Q26=makeQuery(id+"F0.imprint","IMPRINT",FACE,{"disambiguationData":[TD([[makeQuery(id+"F0.imprint","IMPRINT",EDGE,{"disambiguationData":[TD([[subQ6,-1.0]])],"derivedFrom":subQ5}),-1.0]])]});}
            var Q27;
            {var subQ5=sQuery(id+"F0.wireOp",EDGE,"E58");Q27=makeQuery(id+"F0.imprint","IMPRINT",FACE,{"disambiguationData":[TD([[makeQuery(id+"F0.imprint","IMPRINT",EDGE,{"derivedFrom":subQ5}),1.0]])]});}
            var Q28;
            {var subQ3=sQuery(id+"F0.wireOp",EDGE,"E30");var subQ5=sQuery(id+"F0.wireOp",EDGE,"E2");var subQ6=makeQuery(id+"F0.imprint","INTERSECT",VERTEX,{"derivedFrom":[subQ5,subQ3]});Q28=makeQuery(id+"F0.imprint","IMPRINT",FACE,{"disambiguationData":[TD([[makeQuery(id+"F0.imprint","IMPRINT",EDGE,{"disambiguationData":[TD([[subQ6,1.0]])],"derivedFrom":subQ5}),-1.0]])]});}
            var Q29;
            {var subQ5=sQuery(id+"F0.wireOp",EDGE,"E57");Q29=makeQuery(id+"F0.imprint","IMPRINT",FACE,{"disambiguationData":[TD([[makeQuery(id+"F0.imprint","IMPRINT",EDGE,{"derivedFrom":subQ5}),1.0]])]});}
            var Q30;
            {var subQ3=sQuery(id+"F0.wireOp",EDGE,"E63");var subQ5=sQuery(id+"F0.wireOp",EDGE,"E2");var subQ6=makeQuery(id+"F0.imprint","INTERSECT",VERTEX,{"derivedFrom":[subQ5,subQ3]});Q30=makeQuery(id+"F0.imprint","IMPRINT",FACE,{"disambiguationData":[TD([[makeQuery(id+"F0.imprint","IMPRINT",EDGE,{"disambiguationData":[TD([[subQ6,-1.0]])],"derivedFrom":subQ5}),-1.0]])]});}
            var Q31;
            {var subQ5=sQuery(id+"F0.wireOp",EDGE,"E65");Q31=makeQuery(id+"F0.imprint","IMPRINT",FACE,{"disambiguationData":[TD([[makeQuery(id+"F0.imprint","IMPRINT",EDGE,{"derivedFrom":subQ5}),-1.0]])]});}
            var Q32;
            {var subQ0=sQuery(id+"F0.wireOp",EDGE,"E27");var subQ5=sQuery(id+"F0.wireOp",EDGE,"E2");var subQ6=makeQuery(id+"F0.imprint","INTERSECT",VERTEX,{"derivedFrom":[subQ5,subQ0]});Q32=makeQuery(id+"F0.imprint","IMPRINT",FACE,{"disambiguationData":[TD([[makeQuery(id+"F0.imprint","IMPRINT",EDGE,{"disambiguationData":[TD([[subQ6,-1.0]])],"derivedFrom":subQ5}),-1.0]])]});}
            var Q33;
            {var subQ5=sQuery(id+"F0.wireOp",EDGE,"E56");Q33=makeQuery(id+"F0.imprint","IMPRINT",FACE,{"disambiguationData":[TD([[makeQuery(id+"F0.imprint","IMPRINT",EDGE,{"derivedFrom":subQ5}),1.0]])]});}
            var Q34;
            {var subQ0=sQuery(id+"F0.wireOp",EDGE,"E25");var subQ5=sQuery(id+"F0.wireOp",EDGE,"E2");var subQ6=makeQuery(id+"F0.imprint","INTERSECT",VERTEX,{"derivedFrom":[subQ5,subQ0]});Q34=makeQuery(id+"F0.imprint","IMPRINT",FACE,{"disambiguationData":[TD([[makeQuery(id+"F0.imprint","IMPRINT",EDGE,{"disambiguationData":[TD([[subQ6,-1.0]])],"derivedFrom":subQ5}),-1.0]])]});}
            var Q35;
            {var subQ0=sQuery(id+"F0.wireOp",EDGE,"E5");var subQ5=sQuery(id+"F0.wireOp",EDGE,"E2");var subQ6=makeQuery(id+"F0.imprint","INTERSECT",VERTEX,{"derivedFrom":[subQ5,subQ0]});Q35=makeQuery(id+"F0.imprint","IMPRINT",FACE,{"disambiguationData":[TD([[makeQuery(id+"F0.imprint","IMPRINT",EDGE,{"disambiguationData":[TD([[subQ6,-1.0]])],"derivedFrom":subQ5}),-1.0]])]});}
            var Q36;
            {var subQ5=sQuery(id+"F0.wireOp",EDGE,"E55");Q36=makeQuery(id+"F0.imprint","IMPRINT",FACE,{"disambiguationData":[TD([[makeQuery(id+"F0.imprint","IMPRINT",EDGE,{"derivedFrom":subQ5}),1.0]])]});}
            var Q37;
            {var subQ0=sQuery(id+"F0.wireOp",EDGE,"E3");var subQ5=sQuery(id+"F0.wireOp",EDGE,"E2");var subQ6=makeQuery(id+"F0.imprint","INTERSECT",VERTEX,{"derivedFrom":[subQ5,subQ0]});Q37=makeQuery(id+"F0.imprint","IMPRINT",FACE,{"disambiguationData":[TD([[makeQuery(id+"F0.imprint","IMPRINT",EDGE,{"disambiguationData":[TD([[subQ6,-1.0]])],"derivedFrom":subQ5}),-1.0]])]});}
            var Q38;
            {var subQ5=sQuery(id+"F0.wireOp",EDGE,"E54");Q38=makeQuery(id+"F0.imprint","IMPRINT",FACE,{"disambiguationData":[TD([[makeQuery(id+"F0.imprint","IMPRINT",EDGE,{"derivedFrom":subQ5}),1.0]])]});}
            var Q39;
            {var subQ5=sQuery(id+"F0.wireOp",EDGE,"E53");Q39=makeQuery(id+"F0.imprint","IMPRINT",FACE,{"disambiguationData":[TD([[makeQuery(id+"F0.imprint","IMPRINT",EDGE,{"derivedFrom":subQ5}),1.0]])]});}
            extrude(context, id + "F3", {"entities" : qUnion([Q0, Q1, Q2, Q3, Q4, Q5, Q6, Q7, Q8, Q9, Q10, Q11, Q12, Q13, Q14, Q15, Q16, Q17, Q18, Q19, Q20, Q21, Q22, Q23, Q24, Q25, Q26, Q27, Q28, Q29, Q30, Q31, Q32, Q33, Q34, Q35, Q36, Q37, Q38, Q39]), "oppositeDirection" : true, "depth" : 7.11 * mm, "offsetDistance" : 25.4 * mm});
        }
        {
            var Q0;
            {var subQ36=sQuery(id+"F0.wireOp",EDGE,"E67");Q0=makeQuery(id+"F0.imprint","IMPRINT",FACE,{"disambiguationData":[TD([[makeQuery(id+"F0.imprint","IMPRINT",EDGE,{"derivedFrom":subQ36}),-1.0]])]});}
            var Q1;
            {var subQ0=sQuery(id+"F0.wireOp",EDGE,"E43");var subQ1=sQuery(id+"F0.wireOp",EDGE,"E1");var subQ2=makeQuery(id+"F0.imprint","INTERSECT",VERTEX,{"derivedFrom":[subQ1,subQ0]});Q1=makeQuery(id+"F0.imprint","IMPRINT",FACE,{"disambiguationData":[TD([[makeQuery(id+"F0.imprint","IMPRINT",EDGE,{"disambiguationData":[TD([[subQ2,-1.0]])],"derivedFrom":subQ1}),1.0]])]});}
            var Q2;
            {var subQ0=sQuery(id+"F0.wireOp",EDGE,"E23");var subQ1=sQuery(id+"F0.wireOp",EDGE,"E1");var subQ2=makeQuery(id+"F0.imprint","INTERSECT",VERTEX,{"derivedFrom":[subQ1,subQ0]});Q2=makeQuery(id+"F0.imprint","IMPRINT",FACE,{"disambiguationData":[TD([[makeQuery(id+"F0.imprint","IMPRINT",EDGE,{"disambiguationData":[TD([[subQ2,-1.0]])],"derivedFrom":subQ1}),1.0]])]});}
            var Q3;
            {var subQ0=sQuery(id+"F0.wireOp",EDGE,"E21");var subQ1=sQuery(id+"F0.wireOp",EDGE,"E1");var subQ2=makeQuery(id+"F0.imprint","INTERSECT",VERTEX,{"derivedFrom":[subQ1,subQ0]});Q3=makeQuery(id+"F0.imprint","IMPRINT",FACE,{"disambiguationData":[TD([[makeQuery(id+"F0.imprint","IMPRINT",EDGE,{"disambiguationData":[TD([[subQ2,-1.0]])],"derivedFrom":subQ1}),1.0]])]});}
            var Q4;
            {var subQ0=sQuery(id+"F0.wireOp",EDGE,"E19");var subQ1=sQuery(id+"F0.wireOp",EDGE,"E1");var subQ2=makeQuery(id+"F0.imprint","INTERSECT",VERTEX,{"derivedFrom":[subQ1,subQ0]});Q4=makeQuery(id+"F0.imprint","IMPRINT",FACE,{"disambiguationData":[TD([[makeQuery(id+"F0.imprint","IMPRINT",EDGE,{"disambiguationData":[TD([[subQ2,-1.0]])],"derivedFrom":subQ1}),1.0]])]});}
            var Q5;
            {var subQ0=sQuery(id+"F0.wireOp",EDGE,"E17");var subQ1=sQuery(id+"F0.wireOp",EDGE,"E1");var subQ2=makeQuery(id+"F0.imprint","INTERSECT",VERTEX,{"derivedFrom":[subQ1,subQ0]});Q5=makeQuery(id+"F0.imprint","IMPRINT",FACE,{"disambiguationData":[TD([[makeQuery(id+"F0.imprint","IMPRINT",EDGE,{"disambiguationData":[TD([[subQ2,-1.0]])],"derivedFrom":subQ1}),1.0]])]});}
            var Q6;
            {var subQ0=sQuery(id+"F0.wireOp",EDGE,"E14");var subQ1=sQuery(id+"F0.wireOp",EDGE,"E1");var subQ2=makeQuery(id+"F0.imprint","INTERSECT",VERTEX,{"derivedFrom":[subQ1,subQ0]});Q6=makeQuery(id+"F0.imprint","IMPRINT",FACE,{"disambiguationData":[TD([[makeQuery(id+"F0.imprint","IMPRINT",EDGE,{"disambiguationData":[TD([[subQ2,-1.0]])],"derivedFrom":subQ1}),1.0]])]});}
            var Q7;
            {var subQ0=sQuery(id+"F0.wireOp",EDGE,"E11");var subQ1=sQuery(id+"F0.wireOp",EDGE,"E1");var subQ2=makeQuery(id+"F0.imprint","INTERSECT",VERTEX,{"derivedFrom":[subQ1,subQ0]});Q7=makeQuery(id+"F0.imprint","IMPRINT",FACE,{"disambiguationData":[TD([[makeQuery(id+"F0.imprint","IMPRINT",EDGE,{"disambiguationData":[TD([[subQ2,-1.0]])],"derivedFrom":subQ1}),1.0]])]});}
            var Q8;
            {var subQ0=sQuery(id+"F0.wireOp",EDGE,"E3");var subQ1=sQuery(id+"F0.wireOp",EDGE,"E1");var subQ2=makeQuery(id+"F0.imprint","INTERSECT",VERTEX,{"derivedFrom":[subQ1,subQ0]});Q8=makeQuery(id+"F0.imprint","IMPRINT",FACE,{"disambiguationData":[TD([[makeQuery(id+"F0.imprint","IMPRINT",EDGE,{"disambiguationData":[TD([[subQ2,-1.0]])],"derivedFrom":subQ1}),1.0]])]});}
            var Q9;
            {var subQ0=sQuery(id+"F0.wireOp",EDGE,"E8");var subQ1=sQuery(id+"F0.wireOp",EDGE,"E1");var subQ2=makeQuery(id+"F0.imprint","INTERSECT",VERTEX,{"derivedFrom":[subQ1,subQ0]});Q9=makeQuery(id+"F0.imprint","IMPRINT",FACE,{"disambiguationData":[TD([[makeQuery(id+"F0.imprint","IMPRINT",EDGE,{"disambiguationData":[TD([[subQ2,-1.0]])],"derivedFrom":subQ1}),1.0]])]});}
            var Q10;
            {var subQ0=sQuery(id+"F0.wireOp",EDGE,"E5");var subQ1=sQuery(id+"F0.wireOp",EDGE,"E1");var subQ2=makeQuery(id+"F0.imprint","INTERSECT",VERTEX,{"derivedFrom":[subQ1,subQ0]});Q10=makeQuery(id+"F0.imprint","IMPRINT",FACE,{"disambiguationData":[TD([[makeQuery(id+"F0.imprint","IMPRINT",EDGE,{"disambiguationData":[TD([[subQ2,-1.0]])],"derivedFrom":subQ1}),1.0]])]});}
            var Q11;
            {var subQ0=sQuery(id+"F0.wireOp",EDGE,"E25");var subQ1=sQuery(id+"F0.wireOp",EDGE,"E1");var subQ2=makeQuery(id+"F0.imprint","INTERSECT",VERTEX,{"derivedFrom":[subQ1,subQ0]});Q11=makeQuery(id+"F0.imprint","IMPRINT",FACE,{"disambiguationData":[TD([[makeQuery(id+"F0.imprint","IMPRINT",EDGE,{"disambiguationData":[TD([[subQ2,-1.0]])],"derivedFrom":subQ1}),1.0]])]});}
            var Q12;
            {var subQ0=sQuery(id+"F0.wireOp",EDGE,"E64");var subQ1=sQuery(id+"F0.wireOp",EDGE,"E1");var subQ2=makeQuery(id+"F0.imprint","INTERSECT",VERTEX,{"derivedFrom":[subQ1,subQ0]});Q12=makeQuery(id+"F0.imprint","IMPRINT",FACE,{"disambiguationData":[TD([[makeQuery(id+"F0.imprint","IMPRINT",EDGE,{"disambiguationData":[TD([[subQ2,1.0]])],"derivedFrom":subQ1}),1.0]])]});}
            var Q13;
            {var subQ0=sQuery(id+"F0.wireOp",EDGE,"E27");var subQ1=sQuery(id+"F0.wireOp",EDGE,"E1");var subQ2=makeQuery(id+"F0.imprint","INTERSECT",VERTEX,{"derivedFrom":[subQ1,subQ0]});Q13=makeQuery(id+"F0.imprint","IMPRINT",FACE,{"disambiguationData":[TD([[makeQuery(id+"F0.imprint","IMPRINT",EDGE,{"disambiguationData":[TD([[subQ2,-1.0]])],"derivedFrom":subQ1}),1.0]])]});}
            var Q14;
            {var subQ0=sQuery(id+"F0.wireOp",EDGE,"E29");var subQ1=sQuery(id+"F0.wireOp",EDGE,"E1");var subQ2=makeQuery(id+"F0.imprint","INTERSECT",VERTEX,{"derivedFrom":[subQ1,subQ0]});Q14=makeQuery(id+"F0.imprint","IMPRINT",FACE,{"disambiguationData":[TD([[makeQuery(id+"F0.imprint","IMPRINT",EDGE,{"disambiguationData":[TD([[subQ2,-1.0]])],"derivedFrom":subQ1}),1.0]])]});}
            var Q15;
            {var subQ0=sQuery(id+"F0.wireOp",EDGE,"E31");var subQ1=sQuery(id+"F0.wireOp",EDGE,"E1");var subQ2=makeQuery(id+"F0.imprint","INTERSECT",VERTEX,{"derivedFrom":[subQ1,subQ0]});Q15=makeQuery(id+"F0.imprint","IMPRINT",FACE,{"disambiguationData":[TD([[makeQuery(id+"F0.imprint","IMPRINT",EDGE,{"disambiguationData":[TD([[subQ2,-1.0]])],"derivedFrom":subQ1}),1.0]])]});}
            var Q16;
            {var subQ0=sQuery(id+"F0.wireOp",EDGE,"E35");var subQ1=sQuery(id+"F0.wireOp",EDGE,"E1");var subQ2=makeQuery(id+"F0.imprint","INTERSECT",VERTEX,{"derivedFrom":[subQ1,subQ0]});Q16=makeQuery(id+"F0.imprint","IMPRINT",FACE,{"disambiguationData":[TD([[makeQuery(id+"F0.imprint","IMPRINT",EDGE,{"disambiguationData":[TD([[subQ2,-1.0]])],"derivedFrom":subQ1}),1.0]])]});}
            var Q17;
            {var subQ0=sQuery(id+"F0.wireOp",EDGE,"E33");var subQ1=sQuery(id+"F0.wireOp",EDGE,"E1");var subQ2=makeQuery(id+"F0.imprint","INTERSECT",VERTEX,{"derivedFrom":[subQ1,subQ0]});Q17=makeQuery(id+"F0.imprint","IMPRINT",FACE,{"disambiguationData":[TD([[makeQuery(id+"F0.imprint","IMPRINT",EDGE,{"disambiguationData":[TD([[subQ2,-1.0]])],"derivedFrom":subQ1}),1.0]])]});}
            var Q18;
            {var subQ0=sQuery(id+"F0.wireOp",EDGE,"E39");var subQ1=sQuery(id+"F0.wireOp",EDGE,"E1");var subQ2=makeQuery(id+"F0.imprint","INTERSECT",VERTEX,{"derivedFrom":[subQ1,subQ0]});Q18=makeQuery(id+"F0.imprint","IMPRINT",FACE,{"disambiguationData":[TD([[makeQuery(id+"F0.imprint","IMPRINT",EDGE,{"disambiguationData":[TD([[subQ2,-1.0]])],"derivedFrom":subQ1}),1.0]])]});}
            var Q19;
            {var subQ0=sQuery(id+"F0.wireOp",EDGE,"E41");var subQ1=sQuery(id+"F0.wireOp",EDGE,"E1");var subQ2=makeQuery(id+"F0.imprint","INTERSECT",VERTEX,{"derivedFrom":[subQ1,subQ0]});Q19=makeQuery(id+"F0.imprint","IMPRINT",FACE,{"disambiguationData":[TD([[makeQuery(id+"F0.imprint","IMPRINT",EDGE,{"disambiguationData":[TD([[subQ2,-1.0]])],"derivedFrom":subQ1}),1.0]])]});}
            var Q20;
            {var subQ0=sQuery(id+"F0.wireOp",EDGE,"E37");var subQ1=sQuery(id+"F0.wireOp",EDGE,"E1");var subQ2=makeQuery(id+"F0.imprint","INTERSECT",VERTEX,{"derivedFrom":[subQ1,subQ0]});Q20=makeQuery(id+"F0.imprint","IMPRINT",FACE,{"disambiguationData":[TD([[makeQuery(id+"F0.imprint","IMPRINT",EDGE,{"disambiguationData":[TD([[subQ2,-1.0]])],"derivedFrom":subQ1}),1.0]])]});}
            var Q21;
            Q21=makeQuery(id+"F0.imprint","IMPRINT",FACE,{"disambiguationData":[TD([[makeQuery(id+"F0.imprint","IMPRINT",EDGE,{"derivedFrom":sQuery(id+"F0.wireOp",EDGE,"E68")}),1.0]])]});
            var Q22;
            Q22=makeQuery(id+"F0.imprint","IMPRINT",FACE,{"disambiguationData":[TD([[makeQuery(id+"F0.imprint","IMPRINT",EDGE,{"derivedFrom":sQuery(id+"F0.wireOp",EDGE,"E70")}),1.0]])]});
            var Q23;
            Q23=makeQuery(id+"F0.imprint","IMPRINT",FACE,{"disambiguationData":[TD([[makeQuery(id+"F0.imprint","IMPRINT",EDGE,{"derivedFrom":sQuery(id+"F0.wireOp",EDGE,"E71")}),1.0]])]});
            var Q24;
            Q24=makeQuery(id+"F0.imprint","IMPRINT",FACE,{"disambiguationData":[TD([[makeQuery(id+"F0.imprint","IMPRINT",EDGE,{"derivedFrom":sQuery(id+"F0.wireOp",EDGE,"E69")}),1.0]])]});
            var Q25;
            Q25=makeQuery(id+"F0.imprint","IMPRINT",FACE,{"disambiguationData":[TD([[makeQuery(id+"F0.imprint","IMPRINT",EDGE,{"derivedFrom":sQuery(id+"F0.wireOp",EDGE,"E67")}),1.0]])]});
            var Q26;
            {var subQ0=sQuery(id+"F0.wireOp",EDGE,"E66");var subQ4=makeQuery(id+"F0.imprint","INTERSECT",VERTEX,{"derivedFrom":[subQ0,sQuery(id+"F0.wireOp",EDGE,"E68")]});Q26=makeQuery(id+"F0.imprint","IMPRINT",FACE,{"disambiguationData":[TD([[makeQuery(id+"F0.imprint","IMPRINT",EDGE,{"disambiguationData":[TD([[subQ4,1.0]])],"derivedFrom":subQ0}),1.0]])]});}
            var Q27;
            Q27=sQuery(id+"F0.wireOp",EDGE,"E1");
            extrude(context, id + "F4", {"entities" : qUnion([Q0, Q1, Q2, Q3, Q4, Q5, Q6, Q7, Q8, Q9, Q10, Q11, Q12, Q13, Q14, Q15, Q16, Q17, Q18, Q19, Q20, Q21, Q22, Q23, Q24, Q25, Q26]), "surfaceEntities" : qUnion([Q27]), "oppositeDirection" : true, "depth" : 2.03 * mm});
        }
        {
            var Q0;
            Q0=makeQuery(id+"F1.opExtrude","CAP_FACE",FACE,{"disambiguationData":[OSD([sQuery(id+"F0.wireOp",EDGE,"E3"),sQuery(id+"F0.wireOp",EDGE,"E4"),sQuery(id+"F0.wireOp",EDGE,"E5"),sQuery(id+"F0.wireOp",EDGE,"E6"),sQuery(id+"F0.wireOp",EDGE,"E7"),sQuery(id+"F0.wireOp",EDGE,"E8"),sQuery(id+"F0.wireOp",EDGE,"E10"),sQuery(id+"F0.wireOp",EDGE,"E11"),sQuery(id+"F0.wireOp",EDGE,"E13"),sQuery(id+"F0.wireOp",EDGE,"E14"),sQuery(id+"F0.wireOp",EDGE,"E16"),sQuery(id+"F0.wireOp",EDGE,"E17"),sQuery(id+"F0.wireOp",EDGE,"E18"),sQuery(id+"F0.wireOp",EDGE,"E19"),sQuery(id+"F0.wireOp",EDGE,"E20"),sQuery(id+"F0.wireOp",EDGE,"E21"),sQuery(id+"F0.wireOp",EDGE,"E22"),sQuery(id+"F0.wireOp",EDGE,"E23"),sQuery(id+"F0.wireOp",EDGE,"E24"),sQuery(id+"F0.wireOp",EDGE,"E25"),sQuery(id+"F0.wireOp",EDGE,"E26"),sQuery(id+"F0.wireOp",EDGE,"E27"),sQuery(id+"F0.wireOp",EDGE,"E28"),sQuery(id+"F0.wireOp",EDGE,"E29"),sQuery(id+"F0.wireOp",EDGE,"E30"),sQuery(id+"F0.wireOp",EDGE,"E31"),sQuery(id+"F0.wireOp",EDGE,"E32"),sQuery(id+"F0.wireOp",EDGE,"E33"),sQuery(id+"F0.wireOp",EDGE,"E34"),sQuery(id+"F0.wireOp",EDGE,"E35"),sQuery(id+"F0.wireOp",EDGE,"E36"),sQuery(id+"F0.wireOp",EDGE,"E37"),sQuery(id+"F0.wireOp",EDGE,"E38"),sQuery(id+"F0.wireOp",EDGE,"E39"),sQuery(id+"F0.wireOp",EDGE,"E40"),sQuery(id+"F0.wireOp",EDGE,"E41"),sQuery(id+"F0.wireOp",EDGE,"E42"),sQuery(id+"F0.wireOp",EDGE,"E43"),sQuery(id+"F0.wireOp",EDGE,"E44"),sQuery(id+"F0.wireOp",EDGE,"E45"),sQuery(id+"F0.wireOp",EDGE,"E46"),sQuery(id+"F0.wireOp",EDGE,"E47"),sQuery(id+"F0.wireOp",EDGE,"E48"),sQuery(id+"F0.wireOp",EDGE,"E49"),sQuery(id+"F0.wireOp",EDGE,"E50"),sQuery(id+"F0.wireOp",EDGE,"E51"),sQuery(id+"F0.wireOp",EDGE,"E52"),sQuery(id+"F0.wireOp",EDGE,"E53"),sQuery(id+"F0.wireOp",EDGE,"E54"),sQuery(id+"F0.wireOp",EDGE,"E55"),sQuery(id+"F0.wireOp",EDGE,"E56"),sQuery(id+"F0.wireOp",EDGE,"E57"),sQuery(id+"F0.wireOp",EDGE,"E58"),sQuery(id+"F0.wireOp",EDGE,"E59"),sQuery(id+"F0.wireOp",EDGE,"E60"),sQuery(id+"F0.wireOp",EDGE,"E61"),sQuery(id+"F0.wireOp",EDGE,"E62"),sQuery(id+"F0.wireOp",EDGE,"E63"),sQuery(id+"F0.wireOp",EDGE,"E64"),sQuery(id+"F0.wireOp",EDGE,"E65"),sQuery(id+"F0.wireOp",EDGE,"E67"),sQuery(id+"F0.wireOp",EDGE,"E68"),sQuery(id+"F0.wireOp",EDGE,"E69"),sQuery(id+"F0.wireOp",EDGE,"E70"),sQuery(id+"F0.wireOp",EDGE,"E71")])],"isStart":false});
            extrude(context, id + "F5", {"entities" : qUnion([Q0]), "oppositeDirection" : true, "depth" : 1.52 * mm, "offsetDistance" : 25.4 * mm});
        }
    });
